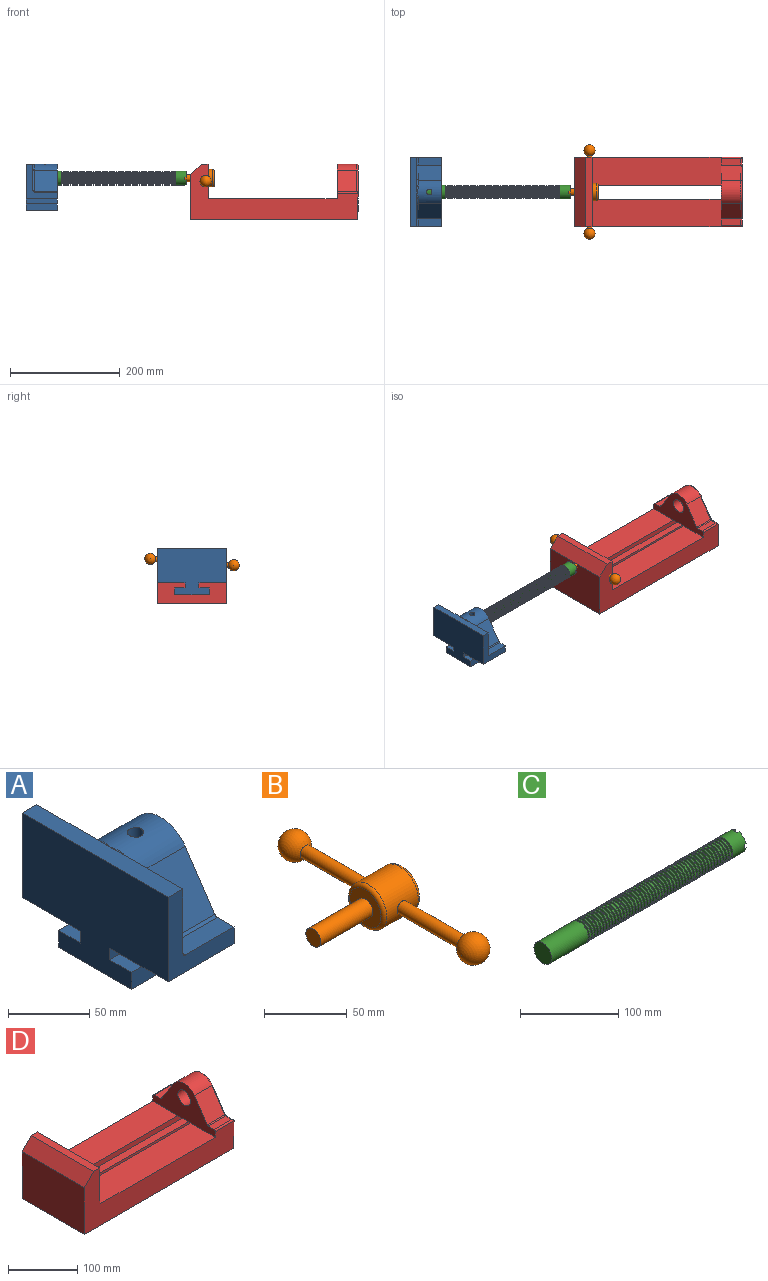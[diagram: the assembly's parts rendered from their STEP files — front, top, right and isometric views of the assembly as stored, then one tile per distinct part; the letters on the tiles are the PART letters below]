
ASSEMBLY  parts=4 mates=3
PART A: 36 faces, bbox 57.2x127x89 mm
  f0: plane 57.15x50.8mm, normal (0,0,-1), area 2903.2mm2, adj f6,f9,f10,f23
  f1: cylinder r=12.7mm len=44.45mm, axis (1,0,0), area 3464.3mm2, adj f6,f15,f16
  f2: plane 41.91x14.52mm, normal (0,0,1), area 608.5mm2, adj f6,f11,f24,f25
  f3: plane 51.86x48.26mm, normal (1,0,0), area 1495.7mm2, adj f8,f10,f31,f33,f35
  f4: plane 51.86x48.26mm, normal (1,0,0), area 1495.7mm2, adj f8,f11,f24,f28,f29
  f5: plane 57.15x50.8mm, normal (0,0,-1), area 2903.2mm2, adj f6,f9,f11,f22
  f6: plane 127x85.09mm, normal (1,0,0), area 5190.6mm2, adj f0,f1,f2,f5,f7,f10,f11,f12
  f7: plane 41.91x14.52mm, normal (0,0,1), area 608.5mm2, adj f6,f10,f30,f31
  f8: plane 127x12.7mm, normal (0,0,1), area 1612.9mm2, adj f3,f4,f9,f10,f11,f26,f34
  f9: plane 127x85.09mm, normal (-1,0,0), area 9096.8mm2, adj f0,f5,f8,f10,f11,f17,f18,f19
  f10: plane 63.5x57.15mm, normal (0,-1,0), area 1372.3mm2, adj f0,f3,f6,f7,f8,f9,f31
  f11: plane 63.5x57.15mm, normal (0,1,0), area 1372.3mm2, adj f2,f4,f5,f6,f8,f9,f24
  f12: plane 41.91x38.43mm, normal (0,-0.83,0.56), area 1939.2mm2, adj f6,f13,f30,f33
  f13: cylinder r=25.4mm len=44.45mm, axis (1,0,0), area 2026.5mm2, adj f6,f12,f14,f16,f26,f28,f34,f35
  f14: plane 41.91x38.43mm, normal (0,0.83,0.56), area 1939.2mm2, adj f6,f13,f25,f29
  f15: plane 25.4x25.4mm, normal (1,0,0), area 506.7mm2, adj f1
  f16: cylinder r=5.08mm len=13.76mm, axis (0,0,1), area 414mm2, adj f1,f13
  f17: plane 57.15x19.05mm, normal (0,0,1), area 1088.7mm2, adj f6,f9,f18,f23
  f18: plane 57.15x12.7mm, normal (0,-1,0), area 725.8mm2, adj f6,f9,f17,f19
  f19: plane 63.5x57.15mm, normal (0,0,-1), area 3629mm2, adj f6,f9,f18,f20
  f20: plane 57.15x12.7mm, normal (0,1,0), area 725.8mm2, adj f6,f9,f19,f21
  f21: plane 57.15x19.05mm, normal (0,0,1), area 1088.7mm2, adj f6,f9,f20,f22
  f22: plane 57.15x8.89mm, normal (0,1,0), area 508.1mm2, adj f5,f6,f9,f21
  f23: plane 57.15x8.89mm, normal (0,-1,0), area 508.1mm2, adj f0,f6,f9,f17
  f24: cylinder r=2.54mm len=14.52mm, axis (0,-1,0), area 57.9mm2, adj f2,f4,f11,f27
  f25: cylinder r=2.54mm len=41.91mm, axis (1,0,0), area 104.3mm2, adj f2,f6,f14,f27
  f26: bspline ~12.24x2.8mm, area 20.9mm2, adj f8,f13,f28
  f27: sphere r=2.54mm, area 6.3mm2, adj f24,f25,f29
  f28: torus R=27.94mm, axis (1,0,0), area 57.8mm2, adj f4,f13,f26,f29
  f29: cylinder r=2.54mm len=39.84mm, axis (0,-0.56,0.83), area 184.6mm2, adj f4,f14,f27,f28
  f30: cylinder r=2.54mm len=41.91mm, axis (1,0,0), area 104.3mm2, adj f6,f7,f12,f32
  f31: cylinder r=2.54mm len=14.52mm, axis (0,-1,0), area 57.9mm2, adj f3,f7,f10,f32
  f32: sphere r=2.54mm, area 6.3mm2, adj f30,f31,f33
  f33: cylinder r=2.54mm len=39.84mm, axis (0,-0.56,-0.83), area 184.6mm2, adj f3,f12,f32,f35
  f34: bspline ~12.24x2.8mm, area 20.9mm2, adj f8,f13,f35
  f35: torus R=27.94mm, axis (1,0,0), area 57.8mm2, adj f3,f13,f33,f34
PART B: 11 faces, bbox 76.2x172.7x34.4 mm
  f0: sphere r=10.16mm, area 1231.8mm2, adj f1
  f1: cylinder r=4.45mm len=51.82mm, axis (0,1,0), area 1438.5mm2, adj f0,f4
  f2: sphere r=10.16mm, area 1231.8mm2, adj f3
  f3: cylinder r=4.45mm len=51.82mm, axis (0,1,0), area 1438.5mm2, adj f2,f4
  f4: cylinder r=15.88mm len=31.75mm, axis (-1,0,0), area 2534.7mm2, adj f1,f3,f9,f10
  f5: cylinder r=6.35mm len=44.45mm, axis (-1,0,0), area 1773.5mm2, adj f6,f8
  f6: plane 12.7x12.7mm, normal (-1,0,0), area 126.7mm2, adj f5
  f7: plane 26.67x26.67mm, normal (1,0,0), area 558.6mm2, adj f10
  f8: plane 26.67x26.67mm, normal (-1,0,0), area 432mm2, adj f5,f9
  f9: torus R=13.33mm, axis (1,0,0), area 374.8mm2, adj f4,f8
  f10: torus R=13.33mm, axis (1,0,0), area 374.8mm2, adj f4,f7
PART C: 220 faces, bbox 279.4x25.4x25.4 mm
  f0: cylinder r=12.7mm len=25.4mm, axis (-1,0,0), area 1468.2mm2, adj f1,f2,f3,f5,f7,f208,f209,f210
  f1: plane 9.9x9.9mm, normal (1,0,0), area 62.3mm2, adj f0,f4,f213,f216
  f2: plane 9.9x9.9mm, normal (1,0,0), area 62.3mm2, adj f0,f4,f210,f218
  f3: plane 9.9x9.9mm, normal (1,0,0), area 62.3mm2, adj f0,f4,f209,f212
  f4: cylinder r=6.35mm len=25.4mm, axis (1,0,0), area 960.3mm2, adj f1,f2,f3,f5,f6,f208,f209,f210
  f5: plane 9.9x9.9mm, normal (1,0,0), area 62.3mm2, adj f0,f4,f215,f217
  f6: plane 12.7x12.7mm, normal (1,0,0), area 126.7mm2, adj f4
  f7: cone r=12.7mm half-angle=76deg, axis (1,0,0), area 188mm2, adj f0,f9
  f8: cone r=10.16mm half-angle=76deg, axis (-1,0,0), area 188mm2, adj f9,f10
  f9: cylinder r=10.16mm len=20.32mm, axis (1,0,0), area 81.1mm2, adj f7,f8
  f10: cylinder r=12.7mm len=25.4mm, axis (-1,0,0), area 131.7mm2, adj f8,f11
  f11: cone r=12.7mm half-angle=76deg, axis (1,0,0), area 188mm2, adj f10,f13
  f12: cone r=10.16mm half-angle=76deg, axis (-1,0,0), area 188mm2, adj f13,f14
  f13: cylinder r=10.16mm len=20.32mm, axis (1,0,0), area 81.1mm2, adj f11,f12
  f14: cylinder r=12.7mm len=25.4mm, axis (-1,0,0), area 131.7mm2, adj f12,f15
  f15: cone r=12.7mm half-angle=76deg, axis (1,0,0), area 188mm2, adj f14,f17
  f16: cone r=10.16mm half-angle=76deg, axis (-1,0,0), area 188mm2, adj f17,f18
  f17: cylinder r=10.16mm len=20.32mm, axis (1,0,0), area 81.1mm2, adj f15,f16
  f18: cylinder r=12.7mm len=25.4mm, axis (-1,0,0), area 131.7mm2, adj f16,f19
  f19: cone r=12.7mm half-angle=76deg, axis (1,0,0), area 188mm2, adj f18,f21
  f20: cone r=10.16mm half-angle=76deg, axis (-1,0,0), area 188mm2, adj f21,f22
  f21: cylinder r=10.16mm len=20.32mm, axis (1,0,0), area 81.1mm2, adj f19,f20
  f22: cylinder r=12.7mm len=25.4mm, axis (-1,0,0), area 131.7mm2, adj f20,f23
  f23: cone r=12.7mm half-angle=76deg, axis (1,0,0), area 188mm2, adj f22,f25
  f24: cone r=10.16mm half-angle=76deg, axis (-1,0,0), area 188mm2, adj f25,f26
  f25: cylinder r=10.16mm len=20.32mm, axis (1,0,0), area 81.1mm2, adj f23,f24
  f26: cylinder r=12.7mm len=25.4mm, axis (-1,0,0), area 131.7mm2, adj f24,f27
  f27: cone r=12.7mm half-angle=76deg, axis (1,0,0), area 188mm2, adj f26,f29
  f28: cone r=10.16mm half-angle=76deg, axis (-1,0,0), area 188mm2, adj f29,f30
  f29: cylinder r=10.16mm len=20.32mm, axis (1,0,0), area 81.1mm2, adj f27,f28
  f30: cylinder r=12.7mm len=25.4mm, axis (-1,0,0), area 131.7mm2, adj f28,f31
  f31: cone r=12.7mm half-angle=76deg, axis (1,0,0), area 188mm2, adj f30,f33
  f32: cone r=10.16mm half-angle=76deg, axis (-1,0,0), area 188mm2, adj f33,f34
  f33: cylinder r=10.16mm len=20.32mm, axis (1,0,0), area 81.1mm2, adj f31,f32
  f34: cylinder r=12.7mm len=25.4mm, axis (-1,0,0), area 131.7mm2, adj f32,f35
  f35: cone r=12.7mm half-angle=76deg, axis (1,0,0), area 188mm2, adj f34,f37
  f36: cone r=10.16mm half-angle=76deg, axis (-1,0,0), area 188mm2, adj f37,f38
  f37: cylinder r=10.16mm len=20.32mm, axis (1,0,0), area 81.1mm2, adj f35,f36
  f38: cylinder r=12.7mm len=25.4mm, axis (-1,0,0), area 131.7mm2, adj f36,f39
  f39: cone r=12.7mm half-angle=76deg, axis (1,0,0), area 188mm2, adj f38,f41
  f40: cone r=10.16mm half-angle=76deg, axis (-1,0,0), area 188mm2, adj f41,f42
  f41: cylinder r=10.16mm len=20.32mm, axis (1,0,0), area 81.1mm2, adj f39,f40
  f42: cylinder r=12.7mm len=25.4mm, axis (-1,0,0), area 131.7mm2, adj f40,f43
  f43: cone r=12.7mm half-angle=76deg, axis (1,0,0), area 188mm2, adj f42,f45
  f44: cone r=10.16mm half-angle=76deg, axis (-1,0,0), area 188mm2, adj f45,f46
  f45: cylinder r=10.16mm len=20.32mm, axis (1,0,0), area 81.1mm2, adj f43,f44
  f46: cylinder r=12.7mm len=25.4mm, axis (-1,0,0), area 131.7mm2, adj f44,f47
  f47: cone r=12.7mm half-angle=76deg, axis (1,0,0), area 188mm2, adj f46,f49
  f48: cone r=10.16mm half-angle=76deg, axis (-1,0,0), area 188mm2, adj f49,f50
  f49: cylinder r=10.16mm len=20.32mm, axis (1,0,0), area 81.1mm2, adj f47,f48
  f50: cylinder r=12.7mm len=25.4mm, axis (-1,0,0), area 131.7mm2, adj f48,f51
  f51: cone r=12.7mm half-angle=76deg, axis (1,0,0), area 188mm2, adj f50,f53
  f52: cone r=10.16mm half-angle=76deg, axis (-1,0,0), area 188mm2, adj f53,f54
  f53: cylinder r=10.16mm len=20.32mm, axis (1,0,0), area 81.1mm2, adj f51,f52
  f54: cylinder r=12.7mm len=25.4mm, axis (-1,0,0), area 131.7mm2, adj f52,f55
  f55: cone r=12.7mm half-angle=76deg, axis (1,0,0), area 188mm2, adj f54,f57
  f56: cone r=10.16mm half-angle=76deg, axis (-1,0,0), area 188mm2, adj f57,f58
  f57: cylinder r=10.16mm len=20.32mm, axis (1,0,0), area 81.1mm2, adj f55,f56
  f58: cylinder r=12.7mm len=25.4mm, axis (-1,0,0), area 131.7mm2, adj f56,f59
  f59: cone r=12.7mm half-angle=76deg, axis (1,0,0), area 188mm2, adj f58,f61
  f60: cone r=10.16mm half-angle=76deg, axis (-1,0,0), area 188mm2, adj f61,f62
  f61: cylinder r=10.16mm len=20.32mm, axis (1,0,0), area 81.1mm2, adj f59,f60
  f62: cylinder r=12.7mm len=25.4mm, axis (-1,0,0), area 131.7mm2, adj f60,f63
  f63: cone r=12.7mm half-angle=76deg, axis (1,0,0), area 188mm2, adj f62,f65
  f64: cone r=10.16mm half-angle=76deg, axis (-1,0,0), area 188mm2, adj f65,f66
  f65: cylinder r=10.16mm len=20.32mm, axis (1,0,0), area 81.1mm2, adj f63,f64
  f66: cylinder r=12.7mm len=25.4mm, axis (-1,0,0), area 131.7mm2, adj f64,f67
  f67: cone r=12.7mm half-angle=76deg, axis (1,0,0), area 188mm2, adj f66,f69
  f68: cone r=10.16mm half-angle=76deg, axis (-1,0,0), area 188mm2, adj f69,f70
  f69: cylinder r=10.16mm len=20.32mm, axis (1,0,0), area 81.1mm2, adj f67,f68
  f70: cylinder r=12.7mm len=25.4mm, axis (-1,0,0), area 131.7mm2, adj f68,f71
  f71: cone r=12.7mm half-angle=76deg, axis (1,0,0), area 188mm2, adj f70,f73
  f72: cone r=10.16mm half-angle=76deg, axis (-1,0,0), area 188mm2, adj f73,f74
  f73: cylinder r=10.16mm len=20.32mm, axis (1,0,0), area 81.1mm2, adj f71,f72
  f74: cylinder r=12.7mm len=25.4mm, axis (-1,0,0), area 131.7mm2, adj f72,f75
  f75: cone r=12.7mm half-angle=76deg, axis (1,0,0), area 188mm2, adj f74,f77
  f76: cone r=10.16mm half-angle=76deg, axis (-1,0,0), area 188mm2, adj f77,f78
  f77: cylinder r=10.16mm len=20.32mm, axis (1,0,0), area 81.1mm2, adj f75,f76
  f78: cylinder r=12.7mm len=25.4mm, axis (-1,0,0), area 131.7mm2, adj f76,f79
  f79: cone r=12.7mm half-angle=76deg, axis (1,0,0), area 188mm2, adj f78,f81
  f80: cone r=10.16mm half-angle=76deg, axis (-1,0,0), area 188mm2, adj f81,f82
  f81: cylinder r=10.16mm len=20.32mm, axis (1,0,0), area 81.1mm2, adj f79,f80
  f82: cylinder r=12.7mm len=25.4mm, axis (-1,0,0), area 131.7mm2, adj f80,f83
  f83: cone r=12.7mm half-angle=76deg, axis (1,0,0), area 188mm2, adj f82,f85
  f84: cone r=10.16mm half-angle=76deg, axis (-1,0,0), area 188mm2, adj f85,f86
  f85: cylinder r=10.16mm len=20.32mm, axis (1,0,0), area 81.1mm2, adj f83,f84
  f86: cylinder r=12.7mm len=25.4mm, axis (-1,0,0), area 131.7mm2, adj f84,f87
  f87: cone r=12.7mm half-angle=76deg, axis (1,0,0), area 188mm2, adj f86,f89
  f88: cone r=10.16mm half-angle=76deg, axis (-1,0,0), area 188mm2, adj f89,f90
  f89: cylinder r=10.16mm len=20.32mm, axis (1,0,0), area 81.1mm2, adj f87,f88
  f90: cylinder r=12.7mm len=25.4mm, axis (-1,0,0), area 131.7mm2, adj f88,f91
  f91: cone r=12.7mm half-angle=76deg, axis (1,0,0), area 188mm2, adj f90,f93
  f92: cone r=10.16mm half-angle=76deg, axis (-1,0,0), area 188mm2, adj f93,f94
  f93: cylinder r=10.16mm len=20.32mm, axis (1,0,0), area 81.1mm2, adj f91,f92
  f94: cylinder r=12.7mm len=25.4mm, axis (-1,0,0), area 131.7mm2, adj f92,f95
  f95: cone r=12.7mm half-angle=76deg, axis (1,0,0), area 188mm2, adj f94,f97
  f96: cone r=10.16mm half-angle=76deg, axis (-1,0,0), area 188mm2, adj f97,f98
  f97: cylinder r=10.16mm len=20.32mm, axis (1,0,0), area 81.1mm2, adj f95,f96
  f98: cylinder r=12.7mm len=25.4mm, axis (-1,0,0), area 131.7mm2, adj f96,f99
  f99: cone r=12.7mm half-angle=76deg, axis (1,0,0), area 188mm2, adj f98,f101
  f100: cone r=10.16mm half-angle=76deg, axis (-1,0,0), area 188mm2, adj f101,f102
  f101: cylinder r=10.16mm len=20.32mm, axis (1,0,0), area 81.1mm2, adj f99,f100
  f102: cylinder r=12.7mm len=25.4mm, axis (-1,0,0), area 131.7mm2, adj f100,f103
  f103: cone r=12.7mm half-angle=76deg, axis (1,0,0), area 188mm2, adj f102,f105
  f104: cone r=10.16mm half-angle=76deg, axis (-1,0,0), area 188mm2, adj f105,f106
  f105: cylinder r=10.16mm len=20.32mm, axis (1,0,0), area 81.1mm2, adj f103,f104
  f106: cylinder r=12.7mm len=25.4mm, axis (-1,0,0), area 131.7mm2, adj f104,f107
  f107: cone r=12.7mm half-angle=76deg, axis (1,0,0), area 188mm2, adj f106,f109
  f108: cone r=10.16mm half-angle=76deg, axis (-1,0,0), area 188mm2, adj f109,f110
  f109: cylinder r=10.16mm len=20.32mm, axis (1,0,0), area 81.1mm2, adj f107,f108
  f110: cylinder r=12.7mm len=25.4mm, axis (-1,0,0), area 131.7mm2, adj f108,f111
  f111: cone r=12.7mm half-angle=76deg, axis (1,0,0), area 188mm2, adj f110,f113
  f112: cone r=10.16mm half-angle=76deg, axis (-1,0,0), area 188mm2, adj f113,f114
  f113: cylinder r=10.16mm len=20.32mm, axis (1,0,0), area 81.1mm2, adj f111,f112
  f114: cylinder r=12.7mm len=25.4mm, axis (-1,0,0), area 131.7mm2, adj f112,f115
  f115: cone r=12.7mm half-angle=76deg, axis (1,0,0), area 188mm2, adj f114,f117
  f116: cone r=10.16mm half-angle=76deg, axis (-1,0,0), area 188mm2, adj f117,f118
  f117: cylinder r=10.16mm len=20.32mm, axis (1,0,0), area 81.1mm2, adj f115,f116
  f118: cylinder r=12.7mm len=25.4mm, axis (-1,0,0), area 131.7mm2, adj f116,f119
  f119: cone r=12.7mm half-angle=76deg, axis (1,0,0), area 188mm2, adj f118,f121
  f120: cone r=10.16mm half-angle=76deg, axis (-1,0,0), area 188mm2, adj f121,f122
  f121: cylinder r=10.16mm len=20.32mm, axis (1,0,0), area 81.1mm2, adj f119,f120
  f122: cylinder r=12.7mm len=25.4mm, axis (-1,0,0), area 131.7mm2, adj f120,f123
  f123: cone r=12.7mm half-angle=76deg, axis (1,0,0), area 188mm2, adj f122,f125
  f124: cone r=10.16mm half-angle=76deg, axis (-1,0,0), area 188mm2, adj f125,f126
  f125: cylinder r=10.16mm len=20.32mm, axis (1,0,0), area 81.1mm2, adj f123,f124
  f126: cylinder r=12.7mm len=25.4mm, axis (-1,0,0), area 131.7mm2, adj f124,f127
  f127: cone r=12.7mm half-angle=76deg, axis (1,0,0), area 188mm2, adj f126,f129
  f128: cone r=10.16mm half-angle=76deg, axis (-1,0,0), area 188mm2, adj f129,f130
  f129: cylinder r=10.16mm len=20.32mm, axis (1,0,0), area 81.1mm2, adj f127,f128
  f130: cylinder r=12.7mm len=25.4mm, axis (-1,0,0), area 131.7mm2, adj f128,f131
  f131: cone r=12.7mm half-angle=76deg, axis (1,0,0), area 188mm2, adj f130,f133
  f132: cone r=10.16mm half-angle=76deg, axis (-1,0,0), area 188mm2, adj f133,f134
  f133: cylinder r=10.16mm len=20.32mm, axis (1,0,0), area 81.1mm2, adj f131,f132
  f134: cylinder r=12.7mm len=25.4mm, axis (-1,0,0), area 131.7mm2, adj f132,f135
  f135: cone r=12.7mm half-angle=76deg, axis (1,0,0), area 188mm2, adj f134,f137
  f136: cone r=10.16mm half-angle=76deg, axis (-1,0,0), area 188mm2, adj f137,f138
  f137: cylinder r=10.16mm len=20.32mm, axis (1,0,0), area 81.1mm2, adj f135,f136
  f138: cylinder r=12.7mm len=25.4mm, axis (-1,0,0), area 131.7mm2, adj f136,f139
  f139: cone r=12.7mm half-angle=76deg, axis (1,0,0), area 188mm2, adj f138,f141
  f140: cone r=10.16mm half-angle=76deg, axis (-1,0,0), area 188mm2, adj f141,f142
  f141: cylinder r=10.16mm len=20.32mm, axis (1,0,0), area 81.1mm2, adj f139,f140
  f142: cylinder r=12.7mm len=25.4mm, axis (-1,0,0), area 131.7mm2, adj f140,f143
  f143: cone r=12.7mm half-angle=76deg, axis (1,0,0), area 188mm2, adj f142,f145
  f144: cone r=10.16mm half-angle=76deg, axis (-1,0,0), area 188mm2, adj f145,f146
  f145: cylinder r=10.16mm len=20.32mm, axis (1,0,0), area 81.1mm2, adj f143,f144
  f146: cylinder r=12.7mm len=25.4mm, axis (-1,0,0), area 131.7mm2, adj f144,f147
  f147: cone r=12.7mm half-angle=76deg, axis (1,0,0), area 188mm2, adj f146,f149
  f148: cone r=10.16mm half-angle=76deg, axis (-1,0,0), area 188mm2, adj f149,f150
  f149: cylinder r=10.16mm len=20.32mm, axis (1,0,0), area 81.1mm2, adj f147,f148
  f150: cylinder r=12.7mm len=25.4mm, axis (-1,0,0), area 131.7mm2, adj f148,f151
  f151: cone r=12.7mm half-angle=76deg, axis (1,0,0), area 188mm2, adj f150,f153
  f152: cone r=10.16mm half-angle=76deg, axis (-1,0,0), area 188mm2, adj f153,f154
  f153: cylinder r=10.16mm len=20.32mm, axis (1,0,0), area 81.1mm2, adj f151,f152
  f154: cylinder r=12.7mm len=25.4mm, axis (-1,0,0), area 131.7mm2, adj f152,f155
  f155: cone r=12.7mm half-angle=76deg, axis (1,0,0), area 188mm2, adj f154,f157
  f156: cone r=10.16mm half-angle=76deg, axis (-1,0,0), area 188mm2, adj f157,f158
  f157: cylinder r=10.16mm len=20.32mm, axis (1,0,0), area 81.1mm2, adj f155,f156
  f158: cylinder r=12.7mm len=25.4mm, axis (-1,0,0), area 131.7mm2, adj f156,f159
  f159: cone r=12.7mm half-angle=76deg, axis (1,0,0), area 188mm2, adj f158,f161
  f160: cone r=10.16mm half-angle=76deg, axis (-1,0,0), area 188mm2, adj f161,f162
  f161: cylinder r=10.16mm len=20.32mm, axis (1,0,0), area 81.1mm2, adj f159,f160
  f162: cylinder r=12.7mm len=25.4mm, axis (-1,0,0), area 131.7mm2, adj f160,f163
  f163: cone r=12.7mm half-angle=76deg, axis (1,0,0), area 188mm2, adj f162,f165
  f164: cone r=10.16mm half-angle=76deg, axis (-1,0,0), area 188mm2, adj f165,f166
  f165: cylinder r=10.16mm len=20.32mm, axis (1,0,0), area 81.1mm2, adj f163,f164
  f166: cylinder r=12.7mm len=25.4mm, axis (-1,0,0), area 131.7mm2, adj f164,f167
  f167: cone r=12.7mm half-angle=76deg, axis (1,0,0), area 188mm2, adj f166,f169
  f168: cone r=10.16mm half-angle=76deg, axis (-1,0,0), area 188mm2, adj f169,f170
  f169: cylinder r=10.16mm len=20.32mm, axis (1,0,0), area 81.1mm2, adj f167,f168
  f170: cylinder r=12.7mm len=25.4mm, axis (-1,0,0), area 131.7mm2, adj f168,f171
  f171: cone r=12.7mm half-angle=76deg, axis (1,0,0), area 188mm2, adj f170,f173
  f172: cone r=10.16mm half-angle=76deg, axis (-1,0,0), area 188mm2, adj f173,f174
  f173: cylinder r=10.16mm len=20.32mm, axis (1,0,0), area 81.1mm2, adj f171,f172
  f174: cylinder r=12.7mm len=25.4mm, axis (-1,0,0), area 131.7mm2, adj f172,f175
  f175: cone r=12.7mm half-angle=76deg, axis (1,0,0), area 188mm2, adj f174,f177
  f176: cone r=10.16mm half-angle=76deg, axis (-1,0,0), area 188mm2, adj f177,f178
  f177: cylinder r=10.16mm len=20.32mm, axis (1,0,0), area 81.1mm2, adj f175,f176
  f178: cylinder r=12.7mm len=25.4mm, axis (-1,0,0), area 131.7mm2, adj f176,f179
  f179: cone r=12.7mm half-angle=76deg, axis (1,0,0), area 188mm2, adj f178,f181
  f180: cone r=10.16mm half-angle=76deg, axis (-1,0,0), area 188mm2, adj f181,f182
  f181: cylinder r=10.16mm len=20.32mm, axis (1,0,0), area 81.1mm2, adj f179,f180
  f182: cylinder r=12.7mm len=25.4mm, axis (-1,0,0), area 131.7mm2, adj f180,f183
  f183: cone r=12.7mm half-angle=76deg, axis (1,0,0), area 188mm2, adj f182,f185
  f184: cone r=10.16mm half-angle=76deg, axis (-1,0,0), area 188mm2, adj f185,f186
  f185: cylinder r=10.16mm len=20.32mm, axis (1,0,0), area 81.1mm2, adj f183,f184
  f186: cylinder r=12.7mm len=25.4mm, axis (-1,0,0), area 131.7mm2, adj f184,f187
  f187: cone r=12.7mm half-angle=76deg, axis (1,0,0), area 188mm2, adj f186,f189
  f188: cone r=10.16mm half-angle=76deg, axis (-1,0,0), area 188mm2, adj f189,f190
  f189: cylinder r=10.16mm len=20.32mm, axis (1,0,0), area 81.1mm2, adj f187,f188
  f190: cylinder r=12.7mm len=25.4mm, axis (-1,0,0), area 131.7mm2, adj f188,f191
  f191: cone r=12.7mm half-angle=76deg, axis (1,0,0), area 188mm2, adj f190,f193
  f192: cone r=10.16mm half-angle=76deg, axis (-1,0,0), area 188mm2, adj f193,f194
  f193: cylinder r=10.16mm len=20.32mm, axis (1,0,0), area 81.1mm2, adj f191,f192
  f194: cylinder r=12.7mm len=25.4mm, axis (-1,0,0), area 131.7mm2, adj f192,f195
  f195: cone r=12.7mm half-angle=76deg, axis (1,0,0), area 188mm2, adj f194,f197
  f196: cone r=10.16mm half-angle=76deg, axis (-1,0,0), area 188mm2, adj f197,f198
  f197: cylinder r=10.16mm len=20.32mm, axis (1,0,0), area 81.1mm2, adj f195,f196
  f198: cylinder r=12.7mm len=25.4mm, axis (-1,0,0), area 131.7mm2, adj f196,f199
  f199: cone r=12.7mm half-angle=76deg, axis (1,0,0), area 188mm2, adj f198,f201
  f200: cone r=10.16mm half-angle=76deg, axis (-1,0,0), area 188mm2, adj f201,f202
  f201: cylinder r=10.16mm len=20.32mm, axis (1,0,0), area 81.1mm2, adj f199,f200
  f202: cylinder r=12.7mm len=25.4mm, axis (-1,0,0), area 131.7mm2, adj f200,f203
  f203: cone r=12.7mm half-angle=76deg, axis (1,0,0), area 188mm2, adj f202,f205
  f204: cone r=10.16mm half-angle=76deg, axis (-1,0,0), area 188mm2, adj f205,f207
  f205: cylinder r=10.16mm len=20.32mm, axis (1,0,0), area 81.1mm2, adj f203,f204
  f206: plane 25.4x25.4mm, normal (-1,0,0), area 506.7mm2, adj f207
  f207: cylinder r=12.7mm len=52.45mm, axis (-1,0,0), area 4185.4mm2, adj f204,f206
  f208: plane 6.88x5.08mm, normal (1,0,0), area 32.7mm2, adj f0,f4,f209,f210
  f209: plane 6.62x2.54mm, normal (0,-1,0), area 16.8mm2, adj f0,f3,f4,f208
  f210: plane 6.62x2.54mm, normal (0,1,0), area 16.8mm2, adj f0,f2,f4,f208
  f211: plane 6.88x5.08mm, normal (1,0,0), area 32.7mm2, adj f0,f4,f212,f213
  f212: plane 6.62x2.54mm, normal (0,0,1), area 16.8mm2, adj f0,f3,f4,f211
  f213: plane 6.62x2.54mm, normal (0,0,-1), area 16.8mm2, adj f0,f1,f4,f211
  f214: plane 6.88x5.08mm, normal (1,0,0), area 32.7mm2, adj f0,f4,f215,f216
  f215: plane 6.62x2.54mm, normal (0,1,0), area 16.8mm2, adj f0,f4,f5,f214
  f216: plane 6.62x2.54mm, normal (0,-1,0), area 16.8mm2, adj f0,f1,f4,f214
  f217: plane 6.62x2.54mm, normal (0,0,-1), area 16.8mm2, adj f0,f4,f5,f219
  f218: plane 6.62x2.54mm, normal (0,0,1), area 16.8mm2, adj f0,f2,f4,f219
  f219: plane 6.88x5.08mm, normal (1,0,0), area 32.7mm2, adj f0,f4,f217,f218
PART D: 39 faces, bbox 304.8x127x103.7 mm
  f0: plane 234.95x50.8mm, normal (0,0,1), area 11935.5mm2, adj f3,f8,f16,f26
  f1: plane 127x99.06mm, normal (1,0,0), area 7097.5mm2, adj f7,f8,f9,f14,f17,f18,f19,f20
  f2: plane 234.95x50.8mm, normal (0,0,1), area 11935.5mm2, adj f3,f9,f16,f27
  f3: plane 127x101.6mm, normal (1,0,0), area 9516.1mm2, adj f0,f2,f4,f7,f8,f9,f18,f19
  f4: plane 127x12.7mm, normal (0,0,1), area 1612.9mm2, adj f3,f5,f8,f9
  f5: plane 127x19.05mm, normal (-0.71,0,0.71), area 3421.5mm2, adj f4,f6,f8,f9
  f6: plane 127x82.55mm, normal (-1,0,0), area 10483.8mm2, adj f5,f7,f8,f9
  f7: plane 304.8x127mm, normal (0,0,-1), area 31774.1mm2, adj f1,f3,f6,f8,f9,f21,f22
  f8: plane 304.8x101.6mm, normal (0,-1,0), area 13834.6mm2, adj f0,f1,f3,f4,f5,f6,f7,f16
  f9: plane 304.8x101.6mm, normal (0,1,0), area 13834.6mm2, adj f1,f2,f3,f4,f5,f6,f7,f16
  f10: plane 35.56x11.98mm, normal (0,0,1), area 426mm2, adj f16,f28,f29,f30
  f11: plane 38.43x35.56mm, normal (0,0.83,0.56), area 1645.4mm2, adj f12,f16,f29,f32
  f12: cylinder r=25.4mm len=42.19mm, axis (1,0,0), area 1770.2mm2, adj f11,f13,f16,f33
  f13: plane 38.43x35.56mm, normal (0,-0.83,0.56), area 1645.4mm2, adj f12,f16,f34,f35
  f14: cylinder r=12.7mm len=38.1mm, axis (1,0,0), area 3040.2mm2, adj f1,f16
  f15: plane 35.56x11.98mm, normal (0,0,1), area 426mm2, adj f16,f34,f36,f38
  f16: plane 127x63.5mm, normal (-1,0,0), area 4155.5mm2, adj f0,f2,f8,f9,f10,f11,f12,f13
  f17: plane 38.1x25.4mm, normal (0,0,-1), area 967.7mm2, adj f1,f16,f26,f27
  f18: plane 273.05x19.05mm, normal (0,0,-1), area 5201.6mm2, adj f1,f3,f19,f26
  f19: plane 273.05x12.7mm, normal (0,1,0), area 3467.7mm2, adj f1,f3,f18,f20
  f20: plane 273.05x19.05mm, normal (0,0,1), area 5201.6mm2, adj f1,f3,f19,f21
  f21: plane 273.05x16.51mm, normal (0,1,0), area 4508.1mm2, adj f1,f3,f7,f20
  f22: plane 273.05x16.51mm, normal (0,-1,0), area 4508.1mm2, adj f1,f3,f7,f23
  f23: plane 273.05x19.05mm, normal (0,0,1), area 5201.6mm2, adj f1,f3,f22,f24
  f24: plane 273.05x12.7mm, normal (0,-1,0), area 3467.7mm2, adj f1,f3,f23,f25
  f25: plane 273.05x19.05mm, normal (0,0,-1), area 5201.6mm2, adj f1,f3,f24,f27
  f26: plane 273.05x8.89mm, normal (0,1,0), area 2427.4mm2, adj f0,f1,f3,f17,f18
  f27: plane 273.05x8.89mm, normal (0,-1,0), area 2427.4mm2, adj f1,f2,f3,f17,f25
  f28: cylinder r=2.54mm len=38.1mm, axis (1,0,0), area 148.3mm2, adj f9,f10,f16,f30
  f29: cylinder r=2.54mm len=35.56mm, axis (-1,0,0), area 88.5mm2, adj f10,f11,f16,f31
  f30: cylinder r=2.54mm len=14.52mm, axis (0,1,0), area 54.3mm2, adj f1,f10,f28,f31
  f31: torus R=5.08mm, axis (-1,0,0), area 13.5mm2, adj f1,f29,f30,f32
  f32: cylinder r=2.54mm len=39.84mm, axis (0,0.56,-0.83), area 184.6mm2, adj f1,f11,f31,f33
  f33: torus R=22.86mm, axis (-1,0,0), area 191.4mm2, adj f1,f12,f32,f35
  f34: cylinder r=2.54mm len=35.56mm, axis (-1,0,0), area 88.5mm2, adj f13,f15,f16,f37
  f35: cylinder r=2.54mm len=39.84mm, axis (0,0.56,0.83), area 184.6mm2, adj f1,f13,f33,f37
  f36: cylinder r=2.54mm len=38.1mm, axis (-1,0,0), area 148.3mm2, adj f8,f15,f16,f38
  f37: torus R=5.08mm, axis (-1,0,0), area 13.5mm2, adj f1,f34,f35,f38
  f38: cylinder r=2.54mm len=14.52mm, axis (0,1,0), area 54.3mm2, adj f1,f15,f36,f37
PLACE A t=(-445.2,-72.74,40.01)mm
PLACE B rot(axis=(1,0,0),4.4deg) t=(-445.2,-66.96,40.23)mm
PLACE C rot(axis=(1,0,0),4.4deg) t=(-445.2,-66.96,40.23)mm
PLACE D t=(-113.38,-72.74,40.01)mm fixed
MATE fastened C.f4 <-> B.f5  axis (1,0,0) through (-451.55,-72.74,116.21)mm
MATE revolute A.f28 <-> C.f7  axis (1,0,0) through (-705.55,-72.74,116.21)mm
MATE slider D.f3 <-> A.f9  axis (-1,0,0) through (-386.43,-136.24,78.11)mm
